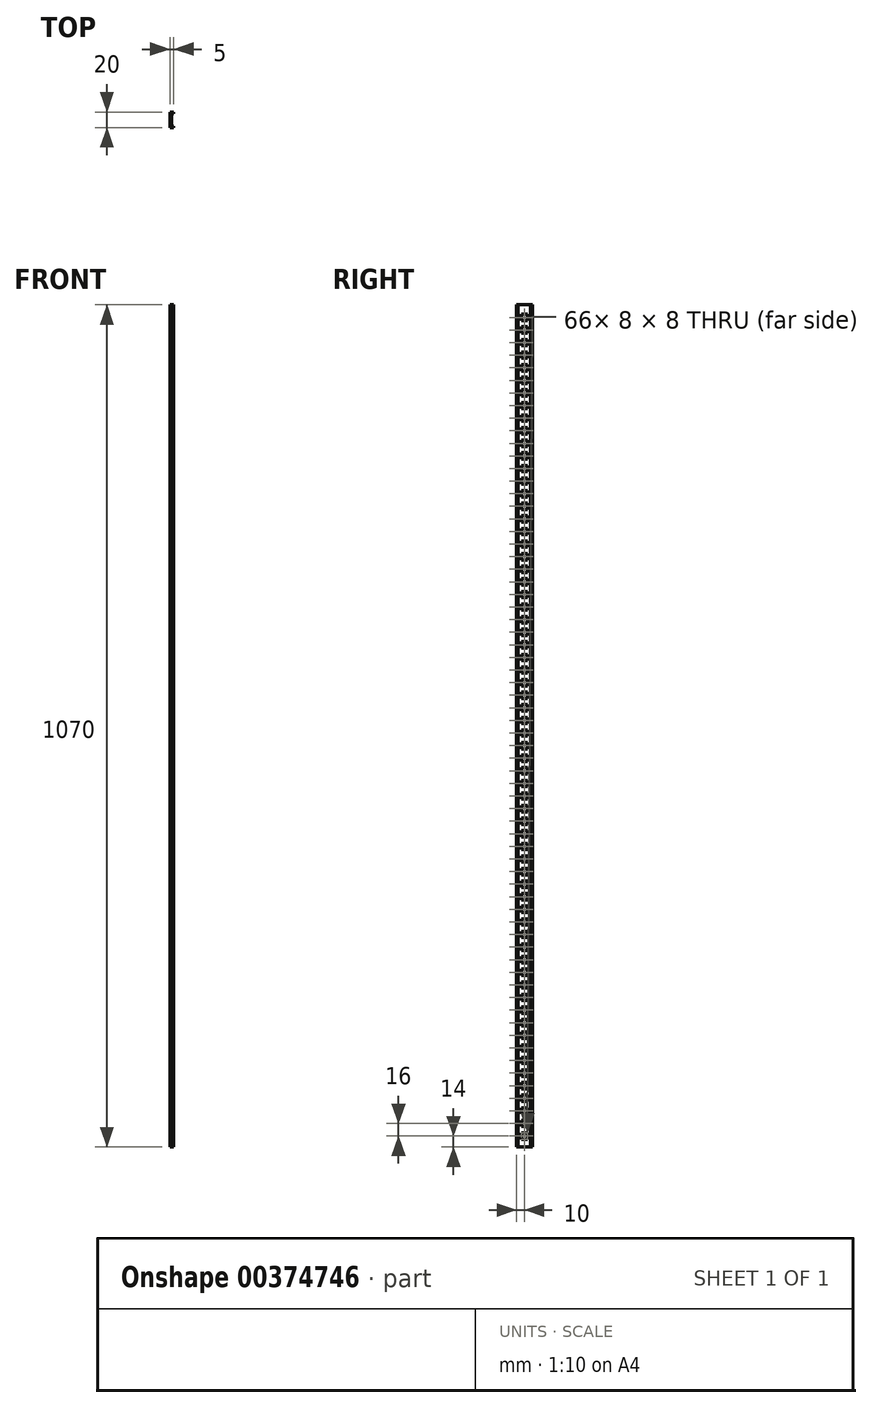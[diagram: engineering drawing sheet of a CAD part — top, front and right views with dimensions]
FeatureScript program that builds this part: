
annotation { "Feature Type Name" : "Feature", "Feature Type Description" : "" }
export const myFeature = defineFeature(function(context is Context, id is Id, definition is map)
    precondition{}
    {
        {
            var Q0;
            Q0=qCreatedBy(makeId("Right.planeOp"),FACE);
            var sketch = newSketch(context, id + "F0", { "sketchPlane" : qUnion([Q0])});
            skLineSegment(sketch, "E0.bottom", {"start": v(-10, 0) * mm, "end": v(10, 0) * mm});
            skLineSegment(sketch, "E0.top", {"start": v(-10, 1070) * mm, "end": v(10, 1070) * mm});
            skLineSegment(sketch, "E0.left", {"start": v(-10, 0) * mm, "end": v(-10, 1070) * mm});
            skLineSegment(sketch, "E0.right", {"start": v(10, 0) * mm, "end": v(10, 1070) * mm});
            skLineSegment(sketch, "E1.bottom", {"start": v(4, 10) * mm, "end": v(-4, 10) * mm});
            skLineSegment(sketch, "E1.top", {"start": v(4, 18) * mm, "end": v(-4, 18) * mm});
            skLineSegment(sketch, "E1.left", {"start": v(4, 10) * mm, "end": v(4, 18) * mm});
            skLineSegment(sketch, "E1.right", {"start": v(-4, 10) * mm, "end": v(-4, 18) * mm});
            skLineSegment(sketch, "E2.1.0.0", {"start": v(4, 26) * mm, "end": v(-4, 26) * mm});
            skLineSegment(sketch, "E2.1.0.1", {"start": v(4, 34) * mm, "end": v(-4, 34) * mm});
            skLineSegment(sketch, "E2.1.0.2", {"start": v(4, 26) * mm, "end": v(4, 34) * mm});
            skLineSegment(sketch, "E2.1.0.3", {"start": v(-4, 26) * mm, "end": v(-4, 34) * mm});
            skLineSegment(sketch, "E2.2.0.0", {"start": v(4, 42) * mm, "end": v(-4, 42) * mm});
            skLineSegment(sketch, "E2.2.0.1", {"start": v(4, 50) * mm, "end": v(-4, 50) * mm});
            skLineSegment(sketch, "E2.2.0.2", {"start": v(4, 42) * mm, "end": v(4, 50) * mm});
            skLineSegment(sketch, "E2.2.0.3", {"start": v(-4, 42) * mm, "end": v(-4, 50) * mm});
            skLineSegment(sketch, "E2.3.0.0", {"start": v(4, 58) * mm, "end": v(-4, 58) * mm});
            skLineSegment(sketch, "E2.3.0.1", {"start": v(4, 66) * mm, "end": v(-4, 66) * mm});
            skLineSegment(sketch, "E2.3.0.2", {"start": v(4, 58) * mm, "end": v(4, 66) * mm});
            skLineSegment(sketch, "E2.3.0.3", {"start": v(-4, 58) * mm, "end": v(-4, 66) * mm});
            skLineSegment(sketch, "E2.4.0.0", {"start": v(4, 74) * mm, "end": v(-4, 74) * mm});
            skLineSegment(sketch, "E2.4.0.1", {"start": v(4, 82) * mm, "end": v(-4, 82) * mm});
            skLineSegment(sketch, "E2.4.0.2", {"start": v(4, 74) * mm, "end": v(4, 82) * mm});
            skLineSegment(sketch, "E2.4.0.3", {"start": v(-4, 74) * mm, "end": v(-4, 82) * mm});
            skLineSegment(sketch, "E2.5.0.0", {"start": v(4, 90) * mm, "end": v(-4, 90) * mm});
            skLineSegment(sketch, "E2.5.0.1", {"start": v(4, 98) * mm, "end": v(-4, 98) * mm});
            skLineSegment(sketch, "E2.5.0.2", {"start": v(4, 90) * mm, "end": v(4, 98) * mm});
            skLineSegment(sketch, "E2.5.0.3", {"start": v(-4, 90) * mm, "end": v(-4, 98) * mm});
            skLineSegment(sketch, "E2.6.0.0", {"start": v(4, 106) * mm, "end": v(-4, 106) * mm});
            skLineSegment(sketch, "E2.6.0.1", {"start": v(4, 114) * mm, "end": v(-4, 114) * mm});
            skLineSegment(sketch, "E2.6.0.2", {"start": v(4, 106) * mm, "end": v(4, 114) * mm});
            skLineSegment(sketch, "E2.6.0.3", {"start": v(-4, 106) * mm, "end": v(-4, 114) * mm});
            skLineSegment(sketch, "E2.7.0.0", {"start": v(4, 122) * mm, "end": v(-4, 122) * mm});
            skLineSegment(sketch, "E2.7.0.1", {"start": v(4, 130) * mm, "end": v(-4, 130) * mm});
            skLineSegment(sketch, "E2.7.0.2", {"start": v(4, 122) * mm, "end": v(4, 130) * mm});
            skLineSegment(sketch, "E2.7.0.3", {"start": v(-4, 122) * mm, "end": v(-4, 130) * mm});
            skLineSegment(sketch, "E2.8.0.0", {"start": v(4, 138) * mm, "end": v(-4, 138) * mm});
            skLineSegment(sketch, "E2.8.0.1", {"start": v(4, 146) * mm, "end": v(-4, 146) * mm});
            skLineSegment(sketch, "E2.8.0.2", {"start": v(4, 138) * mm, "end": v(4, 146) * mm});
            skLineSegment(sketch, "E2.8.0.3", {"start": v(-4, 138) * mm, "end": v(-4, 146) * mm});
            skLineSegment(sketch, "E2.9.0.0", {"start": v(4, 154) * mm, "end": v(-4, 154) * mm});
            skLineSegment(sketch, "E2.9.0.1", {"start": v(4, 162) * mm, "end": v(-4, 162) * mm});
            skLineSegment(sketch, "E2.9.0.2", {"start": v(4, 154) * mm, "end": v(4, 162) * mm});
            skLineSegment(sketch, "E2.9.0.3", {"start": v(-4, 154) * mm, "end": v(-4, 162) * mm});
            skLineSegment(sketch, "E2.10.0.0", {"start": v(4, 170) * mm, "end": v(-4, 170) * mm});
            skLineSegment(sketch, "E2.10.0.1", {"start": v(4, 178) * mm, "end": v(-4, 178) * mm});
            skLineSegment(sketch, "E2.10.0.2", {"start": v(4, 170) * mm, "end": v(4, 178) * mm});
            skLineSegment(sketch, "E2.10.0.3", {"start": v(-4, 170) * mm, "end": v(-4, 178) * mm});
            skLineSegment(sketch, "E2.11.0.0", {"start": v(4, 186) * mm, "end": v(-4, 186) * mm});
            skLineSegment(sketch, "E2.11.0.1", {"start": v(4, 194) * mm, "end": v(-4, 194) * mm});
            skLineSegment(sketch, "E2.11.0.2", {"start": v(4, 186) * mm, "end": v(4, 194) * mm});
            skLineSegment(sketch, "E2.11.0.3", {"start": v(-4, 186) * mm, "end": v(-4, 194) * mm});
            skLineSegment(sketch, "E2.12.0.0", {"start": v(4, 202) * mm, "end": v(-4, 202) * mm});
            skLineSegment(sketch, "E2.12.0.1", {"start": v(4, 210) * mm, "end": v(-4, 210) * mm});
            skLineSegment(sketch, "E2.12.0.2", {"start": v(4, 202) * mm, "end": v(4, 210) * mm});
            skLineSegment(sketch, "E2.12.0.3", {"start": v(-4, 202) * mm, "end": v(-4, 210) * mm});
            skLineSegment(sketch, "E2.13.0.0", {"start": v(4, 218) * mm, "end": v(-4, 218) * mm});
            skLineSegment(sketch, "E2.13.0.1", {"start": v(4, 226) * mm, "end": v(-4, 226) * mm});
            skLineSegment(sketch, "E2.13.0.2", {"start": v(4, 218) * mm, "end": v(4, 226) * mm});
            skLineSegment(sketch, "E2.13.0.3", {"start": v(-4, 218) * mm, "end": v(-4, 226) * mm});
            skLineSegment(sketch, "E2.14.0.0", {"start": v(4, 234) * mm, "end": v(-4, 234) * mm});
            skLineSegment(sketch, "E2.14.0.1", {"start": v(4, 242) * mm, "end": v(-4, 242) * mm});
            skLineSegment(sketch, "E2.14.0.2", {"start": v(4, 234) * mm, "end": v(4, 242) * mm});
            skLineSegment(sketch, "E2.14.0.3", {"start": v(-4, 234) * mm, "end": v(-4, 242) * mm});
            skLineSegment(sketch, "E2.15.0.0", {"start": v(4, 250) * mm, "end": v(-4, 250) * mm});
            skLineSegment(sketch, "E2.15.0.1", {"start": v(4, 258) * mm, "end": v(-4, 258) * mm});
            skLineSegment(sketch, "E2.15.0.2", {"start": v(4, 250) * mm, "end": v(4, 258) * mm});
            skLineSegment(sketch, "E2.15.0.3", {"start": v(-4, 250) * mm, "end": v(-4, 258) * mm});
            skLineSegment(sketch, "E2.16.0.0", {"start": v(4, 266) * mm, "end": v(-4, 266) * mm});
            skLineSegment(sketch, "E2.16.0.1", {"start": v(4, 274) * mm, "end": v(-4, 274) * mm});
            skLineSegment(sketch, "E2.16.0.2", {"start": v(4, 266) * mm, "end": v(4, 274) * mm});
            skLineSegment(sketch, "E2.16.0.3", {"start": v(-4, 266) * mm, "end": v(-4, 274) * mm});
            skLineSegment(sketch, "E2.17.0.0", {"start": v(4, 282) * mm, "end": v(-4, 282) * mm});
            skLineSegment(sketch, "E2.17.0.1", {"start": v(4, 290) * mm, "end": v(-4, 290) * mm});
            skLineSegment(sketch, "E2.17.0.2", {"start": v(4, 282) * mm, "end": v(4, 290) * mm});
            skLineSegment(sketch, "E2.17.0.3", {"start": v(-4, 282) * mm, "end": v(-4, 290) * mm});
            skLineSegment(sketch, "E2.18.0.0", {"start": v(4, 298) * mm, "end": v(-4, 298) * mm});
            skLineSegment(sketch, "E2.18.0.1", {"start": v(4, 306) * mm, "end": v(-4, 306) * mm});
            skLineSegment(sketch, "E2.18.0.2", {"start": v(4, 298) * mm, "end": v(4, 306) * mm});
            skLineSegment(sketch, "E2.18.0.3", {"start": v(-4, 298) * mm, "end": v(-4, 306) * mm});
            skLineSegment(sketch, "E2.19.0.0", {"start": v(4, 314) * mm, "end": v(-4, 314) * mm});
            skLineSegment(sketch, "E2.19.0.1", {"start": v(4, 322) * mm, "end": v(-4, 322) * mm});
            skLineSegment(sketch, "E2.19.0.2", {"start": v(4, 314) * mm, "end": v(4, 322) * mm});
            skLineSegment(sketch, "E2.19.0.3", {"start": v(-4, 314) * mm, "end": v(-4, 322) * mm});
            skLineSegment(sketch, "E2.20.0.0", {"start": v(4, 330) * mm, "end": v(-4, 330) * mm});
            skLineSegment(sketch, "E2.20.0.1", {"start": v(4, 338) * mm, "end": v(-4, 338) * mm});
            skLineSegment(sketch, "E2.20.0.2", {"start": v(4, 330) * mm, "end": v(4, 338) * mm});
            skLineSegment(sketch, "E2.20.0.3", {"start": v(-4, 330) * mm, "end": v(-4, 338) * mm});
            skLineSegment(sketch, "E2.21.0.0", {"start": v(4, 346) * mm, "end": v(-4, 346) * mm});
            skLineSegment(sketch, "E2.21.0.1", {"start": v(4, 354) * mm, "end": v(-4, 354) * mm});
            skLineSegment(sketch, "E2.21.0.2", {"start": v(4, 346) * mm, "end": v(4, 354) * mm});
            skLineSegment(sketch, "E2.21.0.3", {"start": v(-4, 346) * mm, "end": v(-4, 354) * mm});
            skLineSegment(sketch, "E2.22.0.0", {"start": v(4, 362) * mm, "end": v(-4, 362) * mm});
            skLineSegment(sketch, "E2.22.0.1", {"start": v(4, 370) * mm, "end": v(-4, 370) * mm});
            skLineSegment(sketch, "E2.22.0.2", {"start": v(4, 362) * mm, "end": v(4, 370) * mm});
            skLineSegment(sketch, "E2.22.0.3", {"start": v(-4, 362) * mm, "end": v(-4, 370) * mm});
            skLineSegment(sketch, "E2.23.0.0", {"start": v(4, 378) * mm, "end": v(-4, 378) * mm});
            skLineSegment(sketch, "E2.23.0.1", {"start": v(4, 386) * mm, "end": v(-4, 386) * mm});
            skLineSegment(sketch, "E2.23.0.2", {"start": v(4, 378) * mm, "end": v(4, 386) * mm});
            skLineSegment(sketch, "E2.23.0.3", {"start": v(-4, 378) * mm, "end": v(-4, 386) * mm});
            skLineSegment(sketch, "E2.24.0.0", {"start": v(4, 394) * mm, "end": v(-4, 394) * mm});
            skLineSegment(sketch, "E2.24.0.1", {"start": v(4, 402) * mm, "end": v(-4, 402) * mm});
            skLineSegment(sketch, "E2.24.0.2", {"start": v(4, 394) * mm, "end": v(4, 402) * mm});
            skLineSegment(sketch, "E2.24.0.3", {"start": v(-4, 394) * mm, "end": v(-4, 402) * mm});
            skLineSegment(sketch, "E2.25.0.0", {"start": v(4, 410) * mm, "end": v(-4, 410) * mm});
            skLineSegment(sketch, "E2.25.0.1", {"start": v(4, 418) * mm, "end": v(-4, 418) * mm});
            skLineSegment(sketch, "E2.25.0.2", {"start": v(4, 410) * mm, "end": v(4, 418) * mm});
            skLineSegment(sketch, "E2.25.0.3", {"start": v(-4, 410) * mm, "end": v(-4, 418) * mm});
            skLineSegment(sketch, "E2.26.0.0", {"start": v(4, 426) * mm, "end": v(-4, 426) * mm});
            skLineSegment(sketch, "E2.26.0.1", {"start": v(4, 434) * mm, "end": v(-4, 434) * mm});
            skLineSegment(sketch, "E2.26.0.2", {"start": v(4, 426) * mm, "end": v(4, 434) * mm});
            skLineSegment(sketch, "E2.26.0.3", {"start": v(-4, 426) * mm, "end": v(-4, 434) * mm});
            skLineSegment(sketch, "E2.27.0.0", {"start": v(4, 442) * mm, "end": v(-4, 442) * mm});
            skLineSegment(sketch, "E2.27.0.1", {"start": v(4, 450) * mm, "end": v(-4, 450) * mm});
            skLineSegment(sketch, "E2.27.0.2", {"start": v(4, 442) * mm, "end": v(4, 450) * mm});
            skLineSegment(sketch, "E2.27.0.3", {"start": v(-4, 442) * mm, "end": v(-4, 450) * mm});
            skLineSegment(sketch, "E2.28.0.0", {"start": v(4, 458) * mm, "end": v(-4, 458) * mm});
            skLineSegment(sketch, "E2.28.0.1", {"start": v(4, 466) * mm, "end": v(-4, 466) * mm});
            skLineSegment(sketch, "E2.28.0.2", {"start": v(4, 458) * mm, "end": v(4, 466) * mm});
            skLineSegment(sketch, "E2.28.0.3", {"start": v(-4, 458) * mm, "end": v(-4, 466) * mm});
            skLineSegment(sketch, "E2.29.0.0", {"start": v(4, 474) * mm, "end": v(-4, 474) * mm});
            skLineSegment(sketch, "E2.29.0.1", {"start": v(4, 482) * mm, "end": v(-4, 482) * mm});
            skLineSegment(sketch, "E2.29.0.2", {"start": v(4, 474) * mm, "end": v(4, 482) * mm});
            skLineSegment(sketch, "E2.29.0.3", {"start": v(-4, 474) * mm, "end": v(-4, 482) * mm});
            skLineSegment(sketch, "E2.30.0.0", {"start": v(4, 490) * mm, "end": v(-4, 490) * mm});
            skLineSegment(sketch, "E2.30.0.1", {"start": v(4, 498) * mm, "end": v(-4, 498) * mm});
            skLineSegment(sketch, "E2.30.0.2", {"start": v(4, 490) * mm, "end": v(4, 498) * mm});
            skLineSegment(sketch, "E2.30.0.3", {"start": v(-4, 490) * mm, "end": v(-4, 498) * mm});
            skLineSegment(sketch, "E2.31.0.0", {"start": v(4, 506) * mm, "end": v(-4, 506) * mm});
            skLineSegment(sketch, "E2.31.0.1", {"start": v(4, 514) * mm, "end": v(-4, 514) * mm});
            skLineSegment(sketch, "E2.31.0.2", {"start": v(4, 506) * mm, "end": v(4, 514) * mm});
            skLineSegment(sketch, "E2.31.0.3", {"start": v(-4, 506) * mm, "end": v(-4, 514) * mm});
            skLineSegment(sketch, "E2.32.0.0", {"start": v(4, 522) * mm, "end": v(-4, 522) * mm});
            skLineSegment(sketch, "E2.32.0.1", {"start": v(4, 530) * mm, "end": v(-4, 530) * mm});
            skLineSegment(sketch, "E2.32.0.2", {"start": v(4, 522) * mm, "end": v(4, 530) * mm});
            skLineSegment(sketch, "E2.32.0.3", {"start": v(-4, 522) * mm, "end": v(-4, 530) * mm});
            skLineSegment(sketch, "E2.33.0.0", {"start": v(4, 538) * mm, "end": v(-4, 538) * mm});
            skLineSegment(sketch, "E2.33.0.1", {"start": v(4, 546) * mm, "end": v(-4, 546) * mm});
            skLineSegment(sketch, "E2.33.0.2", {"start": v(4, 538) * mm, "end": v(4, 546) * mm});
            skLineSegment(sketch, "E2.33.0.3", {"start": v(-4, 538) * mm, "end": v(-4, 546) * mm});
            skLineSegment(sketch, "E2.34.0.0", {"start": v(4, 554) * mm, "end": v(-4, 554) * mm});
            skLineSegment(sketch, "E2.34.0.1", {"start": v(4, 562) * mm, "end": v(-4, 562) * mm});
            skLineSegment(sketch, "E2.34.0.2", {"start": v(4, 554) * mm, "end": v(4, 562) * mm});
            skLineSegment(sketch, "E2.34.0.3", {"start": v(-4, 554) * mm, "end": v(-4, 562) * mm});
            skLineSegment(sketch, "E2.35.0.0", {"start": v(4, 570) * mm, "end": v(-4, 570) * mm});
            skLineSegment(sketch, "E2.35.0.1", {"start": v(4, 578) * mm, "end": v(-4, 578) * mm});
            skLineSegment(sketch, "E2.35.0.2", {"start": v(4, 570) * mm, "end": v(4, 578) * mm});
            skLineSegment(sketch, "E2.35.0.3", {"start": v(-4, 570) * mm, "end": v(-4, 578) * mm});
            skLineSegment(sketch, "E2.36.0.0", {"start": v(4, 586) * mm, "end": v(-4, 586) * mm});
            skLineSegment(sketch, "E2.36.0.1", {"start": v(4, 594) * mm, "end": v(-4, 594) * mm});
            skLineSegment(sketch, "E2.36.0.2", {"start": v(4, 586) * mm, "end": v(4, 594) * mm});
            skLineSegment(sketch, "E2.36.0.3", {"start": v(-4, 586) * mm, "end": v(-4, 594) * mm});
            skLineSegment(sketch, "E2.37.0.0", {"start": v(4, 602) * mm, "end": v(-4, 602) * mm});
            skLineSegment(sketch, "E2.37.0.1", {"start": v(4, 610) * mm, "end": v(-4, 610) * mm});
            skLineSegment(sketch, "E2.37.0.2", {"start": v(4, 602) * mm, "end": v(4, 610) * mm});
            skLineSegment(sketch, "E2.37.0.3", {"start": v(-4, 602) * mm, "end": v(-4, 610) * mm});
            skLineSegment(sketch, "E2.38.0.0", {"start": v(4, 618) * mm, "end": v(-4, 618) * mm});
            skLineSegment(sketch, "E2.38.0.1", {"start": v(4, 626) * mm, "end": v(-4, 626) * mm});
            skLineSegment(sketch, "E2.38.0.2", {"start": v(4, 618) * mm, "end": v(4, 626) * mm});
            skLineSegment(sketch, "E2.38.0.3", {"start": v(-4, 618) * mm, "end": v(-4, 626) * mm});
            skLineSegment(sketch, "E2.39.0.0", {"start": v(4, 634) * mm, "end": v(-4, 634) * mm});
            skLineSegment(sketch, "E2.39.0.1", {"start": v(4, 642) * mm, "end": v(-4, 642) * mm});
            skLineSegment(sketch, "E2.39.0.2", {"start": v(4, 634) * mm, "end": v(4, 642) * mm});
            skLineSegment(sketch, "E2.39.0.3", {"start": v(-4, 634) * mm, "end": v(-4, 642) * mm});
            skLineSegment(sketch, "E2.40.0.0", {"start": v(4, 650) * mm, "end": v(-4, 650) * mm});
            skLineSegment(sketch, "E2.40.0.1", {"start": v(4, 658) * mm, "end": v(-4, 658) * mm});
            skLineSegment(sketch, "E2.40.0.2", {"start": v(4, 650) * mm, "end": v(4, 658) * mm});
            skLineSegment(sketch, "E2.40.0.3", {"start": v(-4, 650) * mm, "end": v(-4, 658) * mm});
            skLineSegment(sketch, "E2.41.0.0", {"start": v(4, 666) * mm, "end": v(-4, 666) * mm});
            skLineSegment(sketch, "E2.41.0.1", {"start": v(4, 674) * mm, "end": v(-4, 674) * mm});
            skLineSegment(sketch, "E2.41.0.2", {"start": v(4, 666) * mm, "end": v(4, 674) * mm});
            skLineSegment(sketch, "E2.41.0.3", {"start": v(-4, 666) * mm, "end": v(-4, 674) * mm});
            skLineSegment(sketch, "E2.42.0.0", {"start": v(4, 682) * mm, "end": v(-4, 682) * mm});
            skLineSegment(sketch, "E2.42.0.1", {"start": v(4, 690) * mm, "end": v(-4, 690) * mm});
            skLineSegment(sketch, "E2.42.0.2", {"start": v(4, 682) * mm, "end": v(4, 690) * mm});
            skLineSegment(sketch, "E2.42.0.3", {"start": v(-4, 682) * mm, "end": v(-4, 690) * mm});
            skLineSegment(sketch, "E2.43.0.0", {"start": v(4, 698) * mm, "end": v(-4, 698) * mm});
            skLineSegment(sketch, "E2.43.0.1", {"start": v(4, 706) * mm, "end": v(-4, 706) * mm});
            skLineSegment(sketch, "E2.43.0.2", {"start": v(4, 698) * mm, "end": v(4, 706) * mm});
            skLineSegment(sketch, "E2.43.0.3", {"start": v(-4, 698) * mm, "end": v(-4, 706) * mm});
            skLineSegment(sketch, "E2.44.0.0", {"start": v(4, 714) * mm, "end": v(-4, 714) * mm});
            skLineSegment(sketch, "E2.44.0.1", {"start": v(4, 722) * mm, "end": v(-4, 722) * mm});
            skLineSegment(sketch, "E2.44.0.2", {"start": v(4, 714) * mm, "end": v(4, 722) * mm});
            skLineSegment(sketch, "E2.44.0.3", {"start": v(-4, 714) * mm, "end": v(-4, 722) * mm});
            skLineSegment(sketch, "E2.45.0.0", {"start": v(4, 730) * mm, "end": v(-4, 730) * mm});
            skLineSegment(sketch, "E2.45.0.1", {"start": v(4, 738) * mm, "end": v(-4, 738) * mm});
            skLineSegment(sketch, "E2.45.0.2", {"start": v(4, 730) * mm, "end": v(4, 738) * mm});
            skLineSegment(sketch, "E2.45.0.3", {"start": v(-4, 730) * mm, "end": v(-4, 738) * mm});
            skLineSegment(sketch, "E2.46.0.0", {"start": v(4, 746) * mm, "end": v(-4, 746) * mm});
            skLineSegment(sketch, "E2.46.0.1", {"start": v(4, 754) * mm, "end": v(-4, 754) * mm});
            skLineSegment(sketch, "E2.46.0.2", {"start": v(4, 746) * mm, "end": v(4, 754) * mm});
            skLineSegment(sketch, "E2.46.0.3", {"start": v(-4, 746) * mm, "end": v(-4, 754) * mm});
            skLineSegment(sketch, "E2.47.0.0", {"start": v(4, 762) * mm, "end": v(-4, 762) * mm});
            skLineSegment(sketch, "E2.47.0.1", {"start": v(4, 770) * mm, "end": v(-4, 770) * mm});
            skLineSegment(sketch, "E2.47.0.2", {"start": v(4, 762) * mm, "end": v(4, 770) * mm});
            skLineSegment(sketch, "E2.47.0.3", {"start": v(-4, 762) * mm, "end": v(-4, 770) * mm});
            skLineSegment(sketch, "E2.48.0.0", {"start": v(4, 778) * mm, "end": v(-4, 778) * mm});
            skLineSegment(sketch, "E2.48.0.1", {"start": v(4, 786) * mm, "end": v(-4, 786) * mm});
            skLineSegment(sketch, "E2.48.0.2", {"start": v(4, 778) * mm, "end": v(4, 786) * mm});
            skLineSegment(sketch, "E2.48.0.3", {"start": v(-4, 778) * mm, "end": v(-4, 786) * mm});
            skLineSegment(sketch, "E2.49.0.0", {"start": v(4, 794) * mm, "end": v(-4, 794) * mm});
            skLineSegment(sketch, "E2.49.0.1", {"start": v(4, 802) * mm, "end": v(-4, 802) * mm});
            skLineSegment(sketch, "E2.49.0.2", {"start": v(4, 794) * mm, "end": v(4, 802) * mm});
            skLineSegment(sketch, "E2.49.0.3", {"start": v(-4, 794) * mm, "end": v(-4, 802) * mm});
            skLineSegment(sketch, "E2.50.0.0", {"start": v(4, 810) * mm, "end": v(-4, 810) * mm});
            skLineSegment(sketch, "E2.50.0.1", {"start": v(4, 818) * mm, "end": v(-4, 818) * mm});
            skLineSegment(sketch, "E2.50.0.2", {"start": v(4, 810) * mm, "end": v(4, 818) * mm});
            skLineSegment(sketch, "E2.50.0.3", {"start": v(-4, 810) * mm, "end": v(-4, 818) * mm});
            skLineSegment(sketch, "E2.51.0.0", {"start": v(4, 826) * mm, "end": v(-4, 826) * mm});
            skLineSegment(sketch, "E2.51.0.1", {"start": v(4, 834) * mm, "end": v(-4, 834) * mm});
            skLineSegment(sketch, "E2.51.0.2", {"start": v(4, 826) * mm, "end": v(4, 834) * mm});
            skLineSegment(sketch, "E2.51.0.3", {"start": v(-4, 826) * mm, "end": v(-4, 834) * mm});
            skLineSegment(sketch, "E2.52.0.0", {"start": v(4, 842) * mm, "end": v(-4, 842) * mm});
            skLineSegment(sketch, "E2.52.0.1", {"start": v(4, 850) * mm, "end": v(-4, 850) * mm});
            skLineSegment(sketch, "E2.52.0.2", {"start": v(4, 842) * mm, "end": v(4, 850) * mm});
            skLineSegment(sketch, "E2.52.0.3", {"start": v(-4, 842) * mm, "end": v(-4, 850) * mm});
            skLineSegment(sketch, "E2.53.0.0", {"start": v(4, 858) * mm, "end": v(-4, 858) * mm});
            skLineSegment(sketch, "E2.53.0.1", {"start": v(4, 866) * mm, "end": v(-4, 866) * mm});
            skLineSegment(sketch, "E2.53.0.2", {"start": v(4, 858) * mm, "end": v(4, 866) * mm});
            skLineSegment(sketch, "E2.53.0.3", {"start": v(-4, 858) * mm, "end": v(-4, 866) * mm});
            skLineSegment(sketch, "E2.54.0.0", {"start": v(4, 874) * mm, "end": v(-4, 874) * mm});
            skLineSegment(sketch, "E2.54.0.1", {"start": v(4, 882) * mm, "end": v(-4, 882) * mm});
            skLineSegment(sketch, "E2.54.0.2", {"start": v(4, 874) * mm, "end": v(4, 882) * mm});
            skLineSegment(sketch, "E2.54.0.3", {"start": v(-4, 874) * mm, "end": v(-4, 882) * mm});
            skLineSegment(sketch, "E2.55.0.0", {"start": v(4, 890) * mm, "end": v(-4, 890) * mm});
            skLineSegment(sketch, "E2.55.0.1", {"start": v(4, 898) * mm, "end": v(-4, 898) * mm});
            skLineSegment(sketch, "E2.55.0.2", {"start": v(4, 890) * mm, "end": v(4, 898) * mm});
            skLineSegment(sketch, "E2.55.0.3", {"start": v(-4, 890) * mm, "end": v(-4, 898) * mm});
            skLineSegment(sketch, "E2.56.0.0", {"start": v(4, 906) * mm, "end": v(-4, 906) * mm});
            skLineSegment(sketch, "E2.56.0.1", {"start": v(4, 914) * mm, "end": v(-4, 914) * mm});
            skLineSegment(sketch, "E2.56.0.2", {"start": v(4, 906) * mm, "end": v(4, 914) * mm});
            skLineSegment(sketch, "E2.56.0.3", {"start": v(-4, 906) * mm, "end": v(-4, 914) * mm});
            skLineSegment(sketch, "E2.57.0.0", {"start": v(4, 922) * mm, "end": v(-4, 922) * mm});
            skLineSegment(sketch, "E2.57.0.1", {"start": v(4, 930) * mm, "end": v(-4, 930) * mm});
            skLineSegment(sketch, "E2.57.0.2", {"start": v(4, 922) * mm, "end": v(4, 930) * mm});
            skLineSegment(sketch, "E2.57.0.3", {"start": v(-4, 922) * mm, "end": v(-4, 930) * mm});
            skLineSegment(sketch, "E2.58.0.0", {"start": v(4, 938) * mm, "end": v(-4, 938) * mm});
            skLineSegment(sketch, "E2.58.0.1", {"start": v(4, 946) * mm, "end": v(-4, 946) * mm});
            skLineSegment(sketch, "E2.58.0.2", {"start": v(4, 938) * mm, "end": v(4, 946) * mm});
            skLineSegment(sketch, "E2.58.0.3", {"start": v(-4, 938) * mm, "end": v(-4, 946) * mm});
            skLineSegment(sketch, "E2.59.0.0", {"start": v(4, 954) * mm, "end": v(-4, 954) * mm});
            skLineSegment(sketch, "E2.59.0.1", {"start": v(4, 962) * mm, "end": v(-4, 962) * mm});
            skLineSegment(sketch, "E2.59.0.2", {"start": v(4, 954) * mm, "end": v(4, 962) * mm});
            skLineSegment(sketch, "E2.59.0.3", {"start": v(-4, 954) * mm, "end": v(-4, 962) * mm});
            skLineSegment(sketch, "E2.60.0.0", {"start": v(4, 970) * mm, "end": v(-4, 970) * mm});
            skLineSegment(sketch, "E2.60.0.1", {"start": v(4, 978) * mm, "end": v(-4, 978) * mm});
            skLineSegment(sketch, "E2.60.0.2", {"start": v(4, 970) * mm, "end": v(4, 978) * mm});
            skLineSegment(sketch, "E2.60.0.3", {"start": v(-4, 970) * mm, "end": v(-4, 978) * mm});
            skLineSegment(sketch, "E2.61.0.0", {"start": v(4, 986) * mm, "end": v(-4, 986) * mm});
            skLineSegment(sketch, "E2.61.0.1", {"start": v(4, 994) * mm, "end": v(-4, 994) * mm});
            skLineSegment(sketch, "E2.61.0.2", {"start": v(4, 986) * mm, "end": v(4, 994) * mm});
            skLineSegment(sketch, "E2.61.0.3", {"start": v(-4, 986) * mm, "end": v(-4, 994) * mm});
            skLineSegment(sketch, "E2.62.0.0", {"start": v(4, 1002) * mm, "end": v(-4, 1002) * mm});
            skLineSegment(sketch, "E2.62.0.1", {"start": v(4, 1010) * mm, "end": v(-4, 1010) * mm});
            skLineSegment(sketch, "E2.62.0.2", {"start": v(4, 1002) * mm, "end": v(4, 1010) * mm});
            skLineSegment(sketch, "E2.62.0.3", {"start": v(-4, 1002) * mm, "end": v(-4, 1010) * mm});
            skLineSegment(sketch, "E2.63.0.0", {"start": v(4, 1018) * mm, "end": v(-4, 1018) * mm});
            skLineSegment(sketch, "E2.63.0.1", {"start": v(4, 1026) * mm, "end": v(-4, 1026) * mm});
            skLineSegment(sketch, "E2.63.0.2", {"start": v(4, 1018) * mm, "end": v(4, 1026) * mm});
            skLineSegment(sketch, "E2.63.0.3", {"start": v(-4, 1018) * mm, "end": v(-4, 1026) * mm});
            skLineSegment(sketch, "E2.64.0.0", {"start": v(4, 1034) * mm, "end": v(-4, 1034) * mm});
            skLineSegment(sketch, "E2.64.0.1", {"start": v(4, 1042) * mm, "end": v(-4, 1042) * mm});
            skLineSegment(sketch, "E2.64.0.2", {"start": v(4, 1034) * mm, "end": v(4, 1042) * mm});
            skLineSegment(sketch, "E2.64.0.3", {"start": v(-4, 1034) * mm, "end": v(-4, 1042) * mm});
            skLineSegment(sketch, "E2.65.0.0", {"start": v(4, 1050) * mm, "end": v(-4, 1050) * mm});
            skLineSegment(sketch, "E2.65.0.1", {"start": v(4, 1058) * mm, "end": v(-4, 1058) * mm});
            skLineSegment(sketch, "E2.65.0.2", {"start": v(4, 1050) * mm, "end": v(4, 1058) * mm});
            skLineSegment(sketch, "E2.65.0.3", {"start": v(-4, 1050) * mm, "end": v(-4, 1058) * mm});
            skLineSegment(sketch, "E2.direction1", {"start": v(-4, 10) * mm, "end": v(-4, 26) * mm, "construction": true});
            skSolve(sketch);
        }
        {
            var Q0;
            Q0=makeQuery(id+"F0.imprint","IMPRINT",FACE,{"disambiguationData":[TD([[makeQuery(id+"F0.imprint","IMPRINT",EDGE,{"derivedFrom":sQuery(id+"F0.wireOp",EDGE,"E0.bottom")}),1.0]])]});
            extrude(context, id + "F1", {"entities" : qUnion([Q0]), "depth" : 2 * mm});
        }
        {
            var Q0;
            Q0=makeQuery(id+"F1.opExtrude","CAP_FACE",FACE,{"disambiguationData":[OSD([sQuery(id+"F0.wireOp",EDGE,"E0.bottom"),sQuery(id+"F0.wireOp",EDGE,"E0.top"),sQuery(id+"F0.wireOp",EDGE,"E0.left"),sQuery(id+"F0.wireOp",EDGE,"E0.right"),sQuery(id+"F0.wireOp",EDGE,"E1.bottom"),sQuery(id+"F0.wireOp",EDGE,"E1.top"),sQuery(id+"F0.wireOp",EDGE,"E1.left"),sQuery(id+"F0.wireOp",EDGE,"E1.right"),sQuery(id+"F0.wireOp",EDGE,"E2.1.0.0"),sQuery(id+"F0.wireOp",EDGE,"E2.1.0.1"),sQuery(id+"F0.wireOp",EDGE,"E2.1.0.2"),sQuery(id+"F0.wireOp",EDGE,"E2.1.0.3"),sQuery(id+"F0.wireOp",EDGE,"E2.2.0.0"),sQuery(id+"F0.wireOp",EDGE,"E2.2.0.1"),sQuery(id+"F0.wireOp",EDGE,"E2.2.0.2"),sQuery(id+"F0.wireOp",EDGE,"E2.2.0.3"),sQuery(id+"F0.wireOp",EDGE,"E2.3.0.0"),sQuery(id+"F0.wireOp",EDGE,"E2.3.0.1"),sQuery(id+"F0.wireOp",EDGE,"E2.3.0.2"),sQuery(id+"F0.wireOp",EDGE,"E2.3.0.3"),sQuery(id+"F0.wireOp",EDGE,"E2.4.0.0"),sQuery(id+"F0.wireOp",EDGE,"E2.4.0.1"),sQuery(id+"F0.wireOp",EDGE,"E2.4.0.2"),sQuery(id+"F0.wireOp",EDGE,"E2.4.0.3"),sQuery(id+"F0.wireOp",EDGE,"E2.5.0.0"),sQuery(id+"F0.wireOp",EDGE,"E2.5.0.1"),sQuery(id+"F0.wireOp",EDGE,"E2.5.0.2"),sQuery(id+"F0.wireOp",EDGE,"E2.5.0.3"),sQuery(id+"F0.wireOp",EDGE,"E2.6.0.0"),sQuery(id+"F0.wireOp",EDGE,"E2.6.0.1"),sQuery(id+"F0.wireOp",EDGE,"E2.6.0.2"),sQuery(id+"F0.wireOp",EDGE,"E2.6.0.3"),sQuery(id+"F0.wireOp",EDGE,"E2.7.0.0"),sQuery(id+"F0.wireOp",EDGE,"E2.7.0.1"),sQuery(id+"F0.wireOp",EDGE,"E2.7.0.2"),sQuery(id+"F0.wireOp",EDGE,"E2.7.0.3"),sQuery(id+"F0.wireOp",EDGE,"E2.8.0.0"),sQuery(id+"F0.wireOp",EDGE,"E2.8.0.1"),sQuery(id+"F0.wireOp",EDGE,"E2.8.0.2"),sQuery(id+"F0.wireOp",EDGE,"E2.8.0.3"),sQuery(id+"F0.wireOp",EDGE,"E2.9.0.0"),sQuery(id+"F0.wireOp",EDGE,"E2.9.0.1"),sQuery(id+"F0.wireOp",EDGE,"E2.9.0.2"),sQuery(id+"F0.wireOp",EDGE,"E2.9.0.3"),sQuery(id+"F0.wireOp",EDGE,"E2.10.0.0"),sQuery(id+"F0.wireOp",EDGE,"E2.10.0.1"),sQuery(id+"F0.wireOp",EDGE,"E2.10.0.2"),sQuery(id+"F0.wireOp",EDGE,"E2.10.0.3"),sQuery(id+"F0.wireOp",EDGE,"E2.11.0.0"),sQuery(id+"F0.wireOp",EDGE,"E2.11.0.1"),sQuery(id+"F0.wireOp",EDGE,"E2.11.0.2"),sQuery(id+"F0.wireOp",EDGE,"E2.11.0.3"),sQuery(id+"F0.wireOp",EDGE,"E2.12.0.0"),sQuery(id+"F0.wireOp",EDGE,"E2.12.0.1"),sQuery(id+"F0.wireOp",EDGE,"E2.12.0.2"),sQuery(id+"F0.wireOp",EDGE,"E2.12.0.3"),sQuery(id+"F0.wireOp",EDGE,"E2.13.0.0"),sQuery(id+"F0.wireOp",EDGE,"E2.13.0.1"),sQuery(id+"F0.wireOp",EDGE,"E2.13.0.2"),sQuery(id+"F0.wireOp",EDGE,"E2.13.0.3"),sQuery(id+"F0.wireOp",EDGE,"E2.14.0.0"),sQuery(id+"F0.wireOp",EDGE,"E2.14.0.1"),sQuery(id+"F0.wireOp",EDGE,"E2.14.0.2"),sQuery(id+"F0.wireOp",EDGE,"E2.14.0.3"),sQuery(id+"F0.wireOp",EDGE,"E2.15.0.0"),sQuery(id+"F0.wireOp",EDGE,"E2.15.0.1"),sQuery(id+"F0.wireOp",EDGE,"E2.15.0.2"),sQuery(id+"F0.wireOp",EDGE,"E2.15.0.3"),sQuery(id+"F0.wireOp",EDGE,"E2.16.0.0"),sQuery(id+"F0.wireOp",EDGE,"E2.16.0.1"),sQuery(id+"F0.wireOp",EDGE,"E2.16.0.2"),sQuery(id+"F0.wireOp",EDGE,"E2.16.0.3"),sQuery(id+"F0.wireOp",EDGE,"E2.17.0.0"),sQuery(id+"F0.wireOp",EDGE,"E2.17.0.1"),sQuery(id+"F0.wireOp",EDGE,"E2.17.0.2"),sQuery(id+"F0.wireOp",EDGE,"E2.17.0.3"),sQuery(id+"F0.wireOp",EDGE,"E2.18.0.0"),sQuery(id+"F0.wireOp",EDGE,"E2.18.0.1"),sQuery(id+"F0.wireOp",EDGE,"E2.18.0.2"),sQuery(id+"F0.wireOp",EDGE,"E2.18.0.3"),sQuery(id+"F0.wireOp",EDGE,"E2.19.0.0"),sQuery(id+"F0.wireOp",EDGE,"E2.19.0.1"),sQuery(id+"F0.wireOp",EDGE,"E2.19.0.2"),sQuery(id+"F0.wireOp",EDGE,"E2.19.0.3"),sQuery(id+"F0.wireOp",EDGE,"E2.20.0.0"),sQuery(id+"F0.wireOp",EDGE,"E2.20.0.1"),sQuery(id+"F0.wireOp",EDGE,"E2.20.0.2"),sQuery(id+"F0.wireOp",EDGE,"E2.20.0.3"),sQuery(id+"F0.wireOp",EDGE,"E2.21.0.0"),sQuery(id+"F0.wireOp",EDGE,"E2.21.0.1"),sQuery(id+"F0.wireOp",EDGE,"E2.21.0.2"),sQuery(id+"F0.wireOp",EDGE,"E2.21.0.3"),sQuery(id+"F0.wireOp",EDGE,"E2.22.0.0"),sQuery(id+"F0.wireOp",EDGE,"E2.22.0.1"),sQuery(id+"F0.wireOp",EDGE,"E2.22.0.2"),sQuery(id+"F0.wireOp",EDGE,"E2.22.0.3"),sQuery(id+"F0.wireOp",EDGE,"E2.23.0.0"),sQuery(id+"F0.wireOp",EDGE,"E2.23.0.1"),sQuery(id+"F0.wireOp",EDGE,"E2.23.0.2"),sQuery(id+"F0.wireOp",EDGE,"E2.23.0.3"),sQuery(id+"F0.wireOp",EDGE,"E2.24.0.0"),sQuery(id+"F0.wireOp",EDGE,"E2.24.0.1"),sQuery(id+"F0.wireOp",EDGE,"E2.24.0.2"),sQuery(id+"F0.wireOp",EDGE,"E2.24.0.3"),sQuery(id+"F0.wireOp",EDGE,"E2.25.0.0"),sQuery(id+"F0.wireOp",EDGE,"E2.25.0.1"),sQuery(id+"F0.wireOp",EDGE,"E2.25.0.2"),sQuery(id+"F0.wireOp",EDGE,"E2.25.0.3"),sQuery(id+"F0.wireOp",EDGE,"E2.26.0.0"),sQuery(id+"F0.wireOp",EDGE,"E2.26.0.1"),sQuery(id+"F0.wireOp",EDGE,"E2.26.0.2"),sQuery(id+"F0.wireOp",EDGE,"E2.26.0.3"),sQuery(id+"F0.wireOp",EDGE,"E2.27.0.0"),sQuery(id+"F0.wireOp",EDGE,"E2.27.0.1"),sQuery(id+"F0.wireOp",EDGE,"E2.27.0.2"),sQuery(id+"F0.wireOp",EDGE,"E2.27.0.3"),sQuery(id+"F0.wireOp",EDGE,"E2.28.0.0"),sQuery(id+"F0.wireOp",EDGE,"E2.28.0.1"),sQuery(id+"F0.wireOp",EDGE,"E2.28.0.2"),sQuery(id+"F0.wireOp",EDGE,"E2.28.0.3"),sQuery(id+"F0.wireOp",EDGE,"E2.29.0.0"),sQuery(id+"F0.wireOp",EDGE,"E2.29.0.1"),sQuery(id+"F0.wireOp",EDGE,"E2.29.0.2"),sQuery(id+"F0.wireOp",EDGE,"E2.29.0.3"),sQuery(id+"F0.wireOp",EDGE,"E2.30.0.0"),sQuery(id+"F0.wireOp",EDGE,"E2.30.0.1"),sQuery(id+"F0.wireOp",EDGE,"E2.30.0.2"),sQuery(id+"F0.wireOp",EDGE,"E2.30.0.3"),sQuery(id+"F0.wireOp",EDGE,"E2.31.0.0"),sQuery(id+"F0.wireOp",EDGE,"E2.31.0.1"),sQuery(id+"F0.wireOp",EDGE,"E2.31.0.2"),sQuery(id+"F0.wireOp",EDGE,"E2.31.0.3"),sQuery(id+"F0.wireOp",EDGE,"E2.32.0.0"),sQuery(id+"F0.wireOp",EDGE,"E2.32.0.1"),sQuery(id+"F0.wireOp",EDGE,"E2.32.0.2"),sQuery(id+"F0.wireOp",EDGE,"E2.32.0.3"),sQuery(id+"F0.wireOp",EDGE,"E2.33.0.0"),sQuery(id+"F0.wireOp",EDGE,"E2.33.0.1"),sQuery(id+"F0.wireOp",EDGE,"E2.33.0.2"),sQuery(id+"F0.wireOp",EDGE,"E2.33.0.3"),sQuery(id+"F0.wireOp",EDGE,"E2.34.0.0"),sQuery(id+"F0.wireOp",EDGE,"E2.34.0.1"),sQuery(id+"F0.wireOp",EDGE,"E2.34.0.2"),sQuery(id+"F0.wireOp",EDGE,"E2.34.0.3"),sQuery(id+"F0.wireOp",EDGE,"E2.35.0.0"),sQuery(id+"F0.wireOp",EDGE,"E2.35.0.1"),sQuery(id+"F0.wireOp",EDGE,"E2.35.0.2"),sQuery(id+"F0.wireOp",EDGE,"E2.35.0.3"),sQuery(id+"F0.wireOp",EDGE,"E2.36.0.0"),sQuery(id+"F0.wireOp",EDGE,"E2.36.0.1"),sQuery(id+"F0.wireOp",EDGE,"E2.36.0.2"),sQuery(id+"F0.wireOp",EDGE,"E2.36.0.3"),sQuery(id+"F0.wireOp",EDGE,"E2.37.0.0"),sQuery(id+"F0.wireOp",EDGE,"E2.37.0.1"),sQuery(id+"F0.wireOp",EDGE,"E2.37.0.2"),sQuery(id+"F0.wireOp",EDGE,"E2.37.0.3"),sQuery(id+"F0.wireOp",EDGE,"E2.38.0.0"),sQuery(id+"F0.wireOp",EDGE,"E2.38.0.1"),sQuery(id+"F0.wireOp",EDGE,"E2.38.0.2"),sQuery(id+"F0.wireOp",EDGE,"E2.38.0.3"),sQuery(id+"F0.wireOp",EDGE,"E2.39.0.0"),sQuery(id+"F0.wireOp",EDGE,"E2.39.0.1"),sQuery(id+"F0.wireOp",EDGE,"E2.39.0.2"),sQuery(id+"F0.wireOp",EDGE,"E2.39.0.3"),sQuery(id+"F0.wireOp",EDGE,"E2.40.0.0"),sQuery(id+"F0.wireOp",EDGE,"E2.40.0.1"),sQuery(id+"F0.wireOp",EDGE,"E2.40.0.2"),sQuery(id+"F0.wireOp",EDGE,"E2.40.0.3"),sQuery(id+"F0.wireOp",EDGE,"E2.41.0.0"),sQuery(id+"F0.wireOp",EDGE,"E2.41.0.1"),sQuery(id+"F0.wireOp",EDGE,"E2.41.0.2"),sQuery(id+"F0.wireOp",EDGE,"E2.41.0.3"),sQuery(id+"F0.wireOp",EDGE,"E2.42.0.0"),sQuery(id+"F0.wireOp",EDGE,"E2.42.0.1"),sQuery(id+"F0.wireOp",EDGE,"E2.42.0.2"),sQuery(id+"F0.wireOp",EDGE,"E2.42.0.3"),sQuery(id+"F0.wireOp",EDGE,"E2.43.0.0"),sQuery(id+"F0.wireOp",EDGE,"E2.43.0.1"),sQuery(id+"F0.wireOp",EDGE,"E2.43.0.2"),sQuery(id+"F0.wireOp",EDGE,"E2.43.0.3"),sQuery(id+"F0.wireOp",EDGE,"E2.44.0.0"),sQuery(id+"F0.wireOp",EDGE,"E2.44.0.1"),sQuery(id+"F0.wireOp",EDGE,"E2.44.0.2"),sQuery(id+"F0.wireOp",EDGE,"E2.44.0.3"),sQuery(id+"F0.wireOp",EDGE,"E2.45.0.0"),sQuery(id+"F0.wireOp",EDGE,"E2.45.0.1"),sQuery(id+"F0.wireOp",EDGE,"E2.45.0.2"),sQuery(id+"F0.wireOp",EDGE,"E2.45.0.3"),sQuery(id+"F0.wireOp",EDGE,"E2.46.0.0"),sQuery(id+"F0.wireOp",EDGE,"E2.46.0.1"),sQuery(id+"F0.wireOp",EDGE,"E2.46.0.2"),sQuery(id+"F0.wireOp",EDGE,"E2.46.0.3"),sQuery(id+"F0.wireOp",EDGE,"E2.47.0.0"),sQuery(id+"F0.wireOp",EDGE,"E2.47.0.1"),sQuery(id+"F0.wireOp",EDGE,"E2.47.0.2"),sQuery(id+"F0.wireOp",EDGE,"E2.47.0.3"),sQuery(id+"F0.wireOp",EDGE,"E2.48.0.0"),sQuery(id+"F0.wireOp",EDGE,"E2.48.0.1"),sQuery(id+"F0.wireOp",EDGE,"E2.48.0.2"),sQuery(id+"F0.wireOp",EDGE,"E2.48.0.3"),sQuery(id+"F0.wireOp",EDGE,"E2.49.0.0"),sQuery(id+"F0.wireOp",EDGE,"E2.49.0.1"),sQuery(id+"F0.wireOp",EDGE,"E2.49.0.2"),sQuery(id+"F0.wireOp",EDGE,"E2.49.0.3"),sQuery(id+"F0.wireOp",EDGE,"E2.50.0.0"),sQuery(id+"F0.wireOp",EDGE,"E2.50.0.1"),sQuery(id+"F0.wireOp",EDGE,"E2.50.0.2"),sQuery(id+"F0.wireOp",EDGE,"E2.50.0.3"),sQuery(id+"F0.wireOp",EDGE,"E2.51.0.0"),sQuery(id+"F0.wireOp",EDGE,"E2.51.0.1"),sQuery(id+"F0.wireOp",EDGE,"E2.51.0.2"),sQuery(id+"F0.wireOp",EDGE,"E2.51.0.3"),sQuery(id+"F0.wireOp",EDGE,"E2.52.0.0"),sQuery(id+"F0.wireOp",EDGE,"E2.52.0.1"),sQuery(id+"F0.wireOp",EDGE,"E2.52.0.2"),sQuery(id+"F0.wireOp",EDGE,"E2.52.0.3"),sQuery(id+"F0.wireOp",EDGE,"E2.53.0.0"),sQuery(id+"F0.wireOp",EDGE,"E2.53.0.1"),sQuery(id+"F0.wireOp",EDGE,"E2.53.0.2"),sQuery(id+"F0.wireOp",EDGE,"E2.53.0.3"),sQuery(id+"F0.wireOp",EDGE,"E2.54.0.0"),sQuery(id+"F0.wireOp",EDGE,"E2.54.0.1"),sQuery(id+"F0.wireOp",EDGE,"E2.54.0.2"),sQuery(id+"F0.wireOp",EDGE,"E2.54.0.3"),sQuery(id+"F0.wireOp",EDGE,"E2.55.0.0"),sQuery(id+"F0.wireOp",EDGE,"E2.55.0.1"),sQuery(id+"F0.wireOp",EDGE,"E2.55.0.2"),sQuery(id+"F0.wireOp",EDGE,"E2.55.0.3"),sQuery(id+"F0.wireOp",EDGE,"E2.56.0.0"),sQuery(id+"F0.wireOp",EDGE,"E2.56.0.1"),sQuery(id+"F0.wireOp",EDGE,"E2.56.0.2"),sQuery(id+"F0.wireOp",EDGE,"E2.56.0.3"),sQuery(id+"F0.wireOp",EDGE,"E2.57.0.0"),sQuery(id+"F0.wireOp",EDGE,"E2.57.0.1"),sQuery(id+"F0.wireOp",EDGE,"E2.57.0.2"),sQuery(id+"F0.wireOp",EDGE,"E2.57.0.3"),sQuery(id+"F0.wireOp",EDGE,"E2.58.0.0"),sQuery(id+"F0.wireOp",EDGE,"E2.58.0.1"),sQuery(id+"F0.wireOp",EDGE,"E2.58.0.2"),sQuery(id+"F0.wireOp",EDGE,"E2.58.0.3"),sQuery(id+"F0.wireOp",EDGE,"E2.59.0.0"),sQuery(id+"F0.wireOp",EDGE,"E2.59.0.1"),sQuery(id+"F0.wireOp",EDGE,"E2.59.0.2"),sQuery(id+"F0.wireOp",EDGE,"E2.59.0.3"),sQuery(id+"F0.wireOp",EDGE,"E2.60.0.0"),sQuery(id+"F0.wireOp",EDGE,"E2.60.0.1"),sQuery(id+"F0.wireOp",EDGE,"E2.60.0.2"),sQuery(id+"F0.wireOp",EDGE,"E2.60.0.3"),sQuery(id+"F0.wireOp",EDGE,"E2.61.0.0"),sQuery(id+"F0.wireOp",EDGE,"E2.61.0.1"),sQuery(id+"F0.wireOp",EDGE,"E2.61.0.2"),sQuery(id+"F0.wireOp",EDGE,"E2.61.0.3"),sQuery(id+"F0.wireOp",EDGE,"E2.62.0.0"),sQuery(id+"F0.wireOp",EDGE,"E2.62.0.1"),sQuery(id+"F0.wireOp",EDGE,"E2.62.0.2"),sQuery(id+"F0.wireOp",EDGE,"E2.62.0.3"),sQuery(id+"F0.wireOp",EDGE,"E2.63.0.0"),sQuery(id+"F0.wireOp",EDGE,"E2.63.0.1"),sQuery(id+"F0.wireOp",EDGE,"E2.63.0.2"),sQuery(id+"F0.wireOp",EDGE,"E2.63.0.3"),sQuery(id+"F0.wireOp",EDGE,"E2.64.0.0"),sQuery(id+"F0.wireOp",EDGE,"E2.64.0.1"),sQuery(id+"F0.wireOp",EDGE,"E2.64.0.2"),sQuery(id+"F0.wireOp",EDGE,"E2.64.0.3"),sQuery(id+"F0.wireOp",EDGE,"E2.65.0.0"),sQuery(id+"F0.wireOp",EDGE,"E2.65.0.1"),sQuery(id+"F0.wireOp",EDGE,"E2.65.0.2"),sQuery(id+"F0.wireOp",EDGE,"E2.65.0.3"),sQuery(id+"F0.wireOp",EDGE,"E2.66.0.0"),sQuery(id+"F0.wireOp",EDGE,"E2.66.0.1"),sQuery(id+"F0.wireOp",EDGE,"E2.66.0.2"),sQuery(id+"F0.wireOp",EDGE,"E2.66.0.3"),sQuery(id+"F0.wireOp",EDGE,"E2.67.0.0"),sQuery(id+"F0.wireOp",EDGE,"E2.67.0.1"),sQuery(id+"F0.wireOp",EDGE,"E2.67.0.2"),sQuery(id+"F0.wireOp",EDGE,"E2.67.0.3"),sQuery(id+"F0.wireOp",EDGE,"E2.68.0.0"),sQuery(id+"F0.wireOp",EDGE,"E2.68.0.1"),sQuery(id+"F0.wireOp",EDGE,"E2.68.0.2"),sQuery(id+"F0.wireOp",EDGE,"E2.68.0.3"),sQuery(id+"F0.wireOp",EDGE,"E2.69.0.0"),sQuery(id+"F0.wireOp",EDGE,"E2.69.0.1"),sQuery(id+"F0.wireOp",EDGE,"E2.69.0.2"),sQuery(id+"F0.wireOp",EDGE,"E2.69.0.3"),sQuery(id+"F0.wireOp",EDGE,"E2.70.0.0"),sQuery(id+"F0.wireOp",EDGE,"E2.70.0.1"),sQuery(id+"F0.wireOp",EDGE,"E2.70.0.2"),sQuery(id+"F0.wireOp",EDGE,"E2.70.0.3"),sQuery(id+"F0.wireOp",EDGE,"E2.71.0.0"),sQuery(id+"F0.wireOp",EDGE,"E2.71.0.1"),sQuery(id+"F0.wireOp",EDGE,"E2.71.0.2"),sQuery(id+"F0.wireOp",EDGE,"E2.71.0.3")])],"isStart":false});
            var sketch = newSketch(context, id + "F2", { "sketchPlane" : qUnion([Q0])});
            skLineSegment(sketch, "E3.bottom", {"start": v(10, 1070) * mm, "end": v(8, 1070) * mm});
            skLineSegment(sketch, "E3.top", {"start": v(10, 0) * mm, "end": v(8, 0) * mm});
            skLineSegment(sketch, "E3.left", {"start": v(10, 1070) * mm, "end": v(10, 0) * mm});
            skLineSegment(sketch, "E3.right", {"start": v(8, 1070) * mm, "end": v(8, 0) * mm});
            skLineSegment(sketch, "E4.bottom", {"start": v(-10, 0) * mm, "end": v(-8, 0) * mm});
            skLineSegment(sketch, "E4.top", {"start": v(-10, 1070) * mm, "end": v(-8, 1070) * mm});
            skLineSegment(sketch, "E4.left", {"start": v(-10, 0) * mm, "end": v(-10, 1070) * mm});
            skLineSegment(sketch, "E4.right", {"start": v(-8, 0) * mm, "end": v(-8, 1070) * mm});
            skSolve(sketch);
        }
        {
            var Q0;
            Q0=makeQuery(id+"F2.imprint","IMPRINT",FACE,{"disambiguationData":[TD([[makeQuery(id+"F2.imprint","IMPRINT",EDGE,{"derivedFrom":sQuery(id+"F2.wireOp",EDGE,"E4.bottom")}),1.0]])]});
            var Q1;
            Q1=makeQuery(id+"F2.imprint","IMPRINT",FACE,{"disambiguationData":[TD([[makeQuery(id+"F2.imprint","IMPRINT",EDGE,{"derivedFrom":sQuery(id+"F2.wireOp",EDGE,"E3.bottom")}),-1.0]])]});
            extrude(context, id + "F3", {"entities" : qUnion([Q0, Q1]), "operationType" : NewBodyOperationType.ADD, "depth" : 3 * mm});
        }
    });
